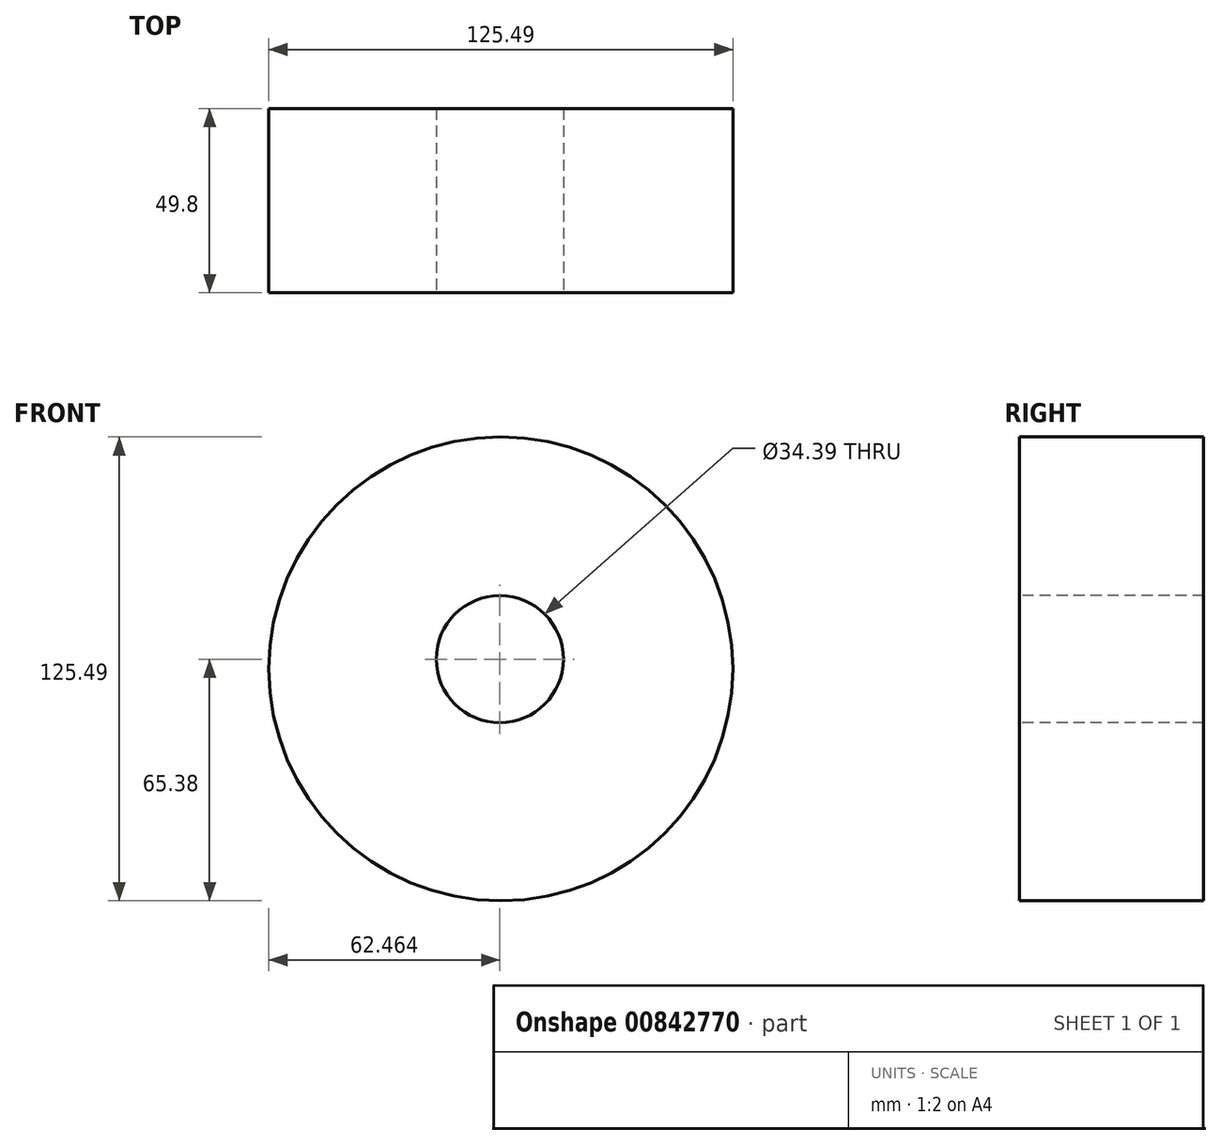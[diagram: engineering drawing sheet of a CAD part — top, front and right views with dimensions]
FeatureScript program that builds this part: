
annotation { "Feature Type Name" : "Feature", "Feature Type Description" : "" }
export const myFeature = defineFeature(function(context is Context, id is Id, definition is map)
    precondition{}
    {
        {
            var Q0;
            Q0=qCreatedBy(makeId("Front.planeOp"),FACE);
            var sketch = newSketch(context, id + "F0", { "sketchPlane" : qUnion([Q0])});
            skCircle(sketch, "E0", {"center": v(-7.44, 7.4) * mm, "radius": 62.75 * mm});
            skSolve(sketch);
        }
        {
            var Q0;
            Q0=makeQuery(id+"F0.imprint","IMPRINT",FACE,{"disambiguationData":[TD([[makeQuery(id+"F0.imprint","IMPRINT",EDGE,{"derivedFrom":sQuery(id+"F0.wireOp",EDGE,"E0")}),1.0]])]});
            extrude(context, id + "F1", {"entities" : qUnion([Q0]), "depth" : 49.8 * mm, "offsetDistance" : 25.4 * mm});
        }
        {
            var Q0;
            Q0=makeQuery(id+"F1.opExtrude","CAP_FACE",FACE,{"disambiguationData":[OSD([sQuery(id+"F0.wireOp",EDGE,"E0")])],"isStart":false});
            var sketch = newSketch(context, id + "F2", { "sketchPlane" : qUnion([Q0])});
            skCircle(sketch, "E1", {"center": v(-7.73, 10.03) * mm, "radius": 17.2 * mm});
            skSolve(sketch);
        }
        {
            var Q0;
            Q0=makeQuery(id+"F2.imprint","IMPRINT",FACE,{"disambiguationData":[TD([[makeQuery(id+"F2.imprint","IMPRINT",EDGE,{"derivedFrom":sQuery(id+"F2.wireOp",EDGE,"E1")}),1.0]])]});
            var Q1;
            Q1=makeQuery(id+"F1.opExtrude","CAP_FACE",FACE,{"disambiguationData":[OSD([sQuery(id+"F0.wireOp",EDGE,"E0")])],"isStart":true});
            extrude(context, id + "F3", {"entities" : qUnion([Q0, Q1]), "operationType" : NewBodyOperationType.REMOVE, "oppositeDirection" : true, "depth" : 57.8 * mm, "offsetDistance" : 25 * mm});
        }
    });
